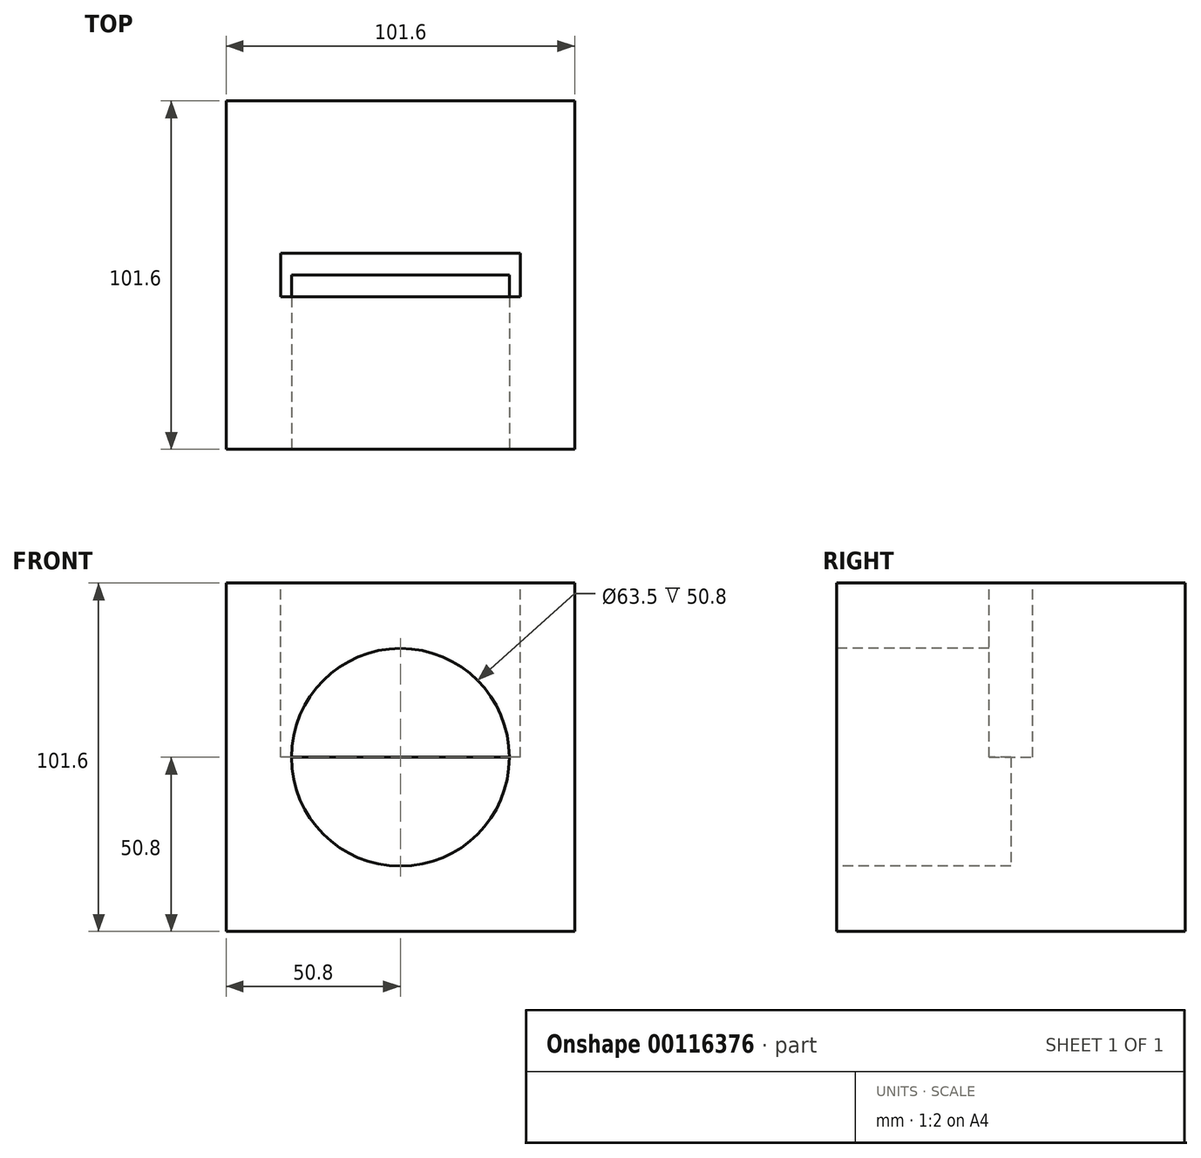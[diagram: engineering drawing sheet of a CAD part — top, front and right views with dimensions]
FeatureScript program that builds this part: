
annotation { "Feature Type Name" : "Feature", "Feature Type Description" : "" }
export const myFeature = defineFeature(function(context is Context, id is Id, definition is map)
    precondition{}
    {
        {
            var Q0;
            Q0=qCreatedBy(makeId("Front.planeOp"),FACE);
            var sketch = newSketch(context, id + "F0", { "sketchPlane" : qUnion([Q0])});
            skLineSegment(sketch, "E0.bottom", {"start": v(50.8, -50.8) * mm, "end": v(-50.8, -50.8) * mm});
            skLineSegment(sketch, "E0.top", {"start": v(50.8, 50.8) * mm, "end": v(-50.8, 50.8) * mm});
            skLineSegment(sketch, "E0.left", {"start": v(50.8, -50.8) * mm, "end": v(50.8, 50.8) * mm});
            skLineSegment(sketch, "E0.right", {"start": v(-50.8, -50.8) * mm, "end": v(-50.8, 50.8) * mm});
            skPoint(sketch, "E0.middle", {"position": v(0, 0) * mm});
            skSolve(sketch);
        }
        {
            var Q0;
            Q0 = qSketchRegion(id + "F0", true);
            extrude(context, id + "F1", {"entities" : qUnion([Q0]), "endBound" : BoundingType.SYMMETRIC, "depth" : 101.6 * mm});
        }
        {
            var Q0;
            Q0=makeQuery(id+"F1.opExtrude","SWEPT_FACE",FACE,{"disambiguationData":[OSD([sQuery(id+"F0.wireOp",EDGE,"E0.top")])]});
            var sketch = newSketch(context, id + "F2", { "sketchPlane" : qUnion([Q0])});
            skLineSegment(sketch, "E1.bottom", {"start": v(34.93, -6.35) * mm, "end": v(-34.93, -6.35) * mm});
            skLineSegment(sketch, "E1.top", {"start": v(34.93, 6.35) * mm, "end": v(-34.93, 6.35) * mm});
            skLineSegment(sketch, "E1.left", {"start": v(34.93, -6.35) * mm, "end": v(34.93, 6.35) * mm});
            skLineSegment(sketch, "E1.right", {"start": v(-34.93, -6.35) * mm, "end": v(-34.93, 6.35) * mm});
            skPoint(sketch, "E1.middle", {"position": v(0, 0) * mm});
            skSolve(sketch);
        }
        {
            var Q0;
            Q0 = qSketchRegion(id + "F2", true);
            extrude(context, id + "F3", {"entities" : qUnion([Q0]), "operationType" : NewBodyOperationType.REMOVE, "oppositeDirection" : true, "depth" : 50.8 * mm});
        }
        {
            var Q0;
            Q0=makeQuery(id+"F1.opExtrude","CAP_FACE",FACE,{"disambiguationData":[OSD([sQuery(id+"F0.wireOp",EDGE,"E0.bottom"),sQuery(id+"F0.wireOp",EDGE,"E0.top"),sQuery(id+"F0.wireOp",EDGE,"E0.left"),sQuery(id+"F0.wireOp",EDGE,"E0.right")])],"isStart":false});
            var sketch = newSketch(context, id + "F4", { "sketchPlane" : qUnion([Q0])});
            skCircle(sketch, "E2", {"center": v(0, 0) * mm, "radius": 31.75 * mm});
            skSolve(sketch);
        }
        {
            var Q0;
            Q0 = qSketchRegion(id + "F4", true);
            extrude(context, id + "F5", {"entities" : qUnion([Q0]), "operationType" : NewBodyOperationType.REMOVE, "oppositeDirection" : true, "depth" : 50.8 * mm});
        }
    });
